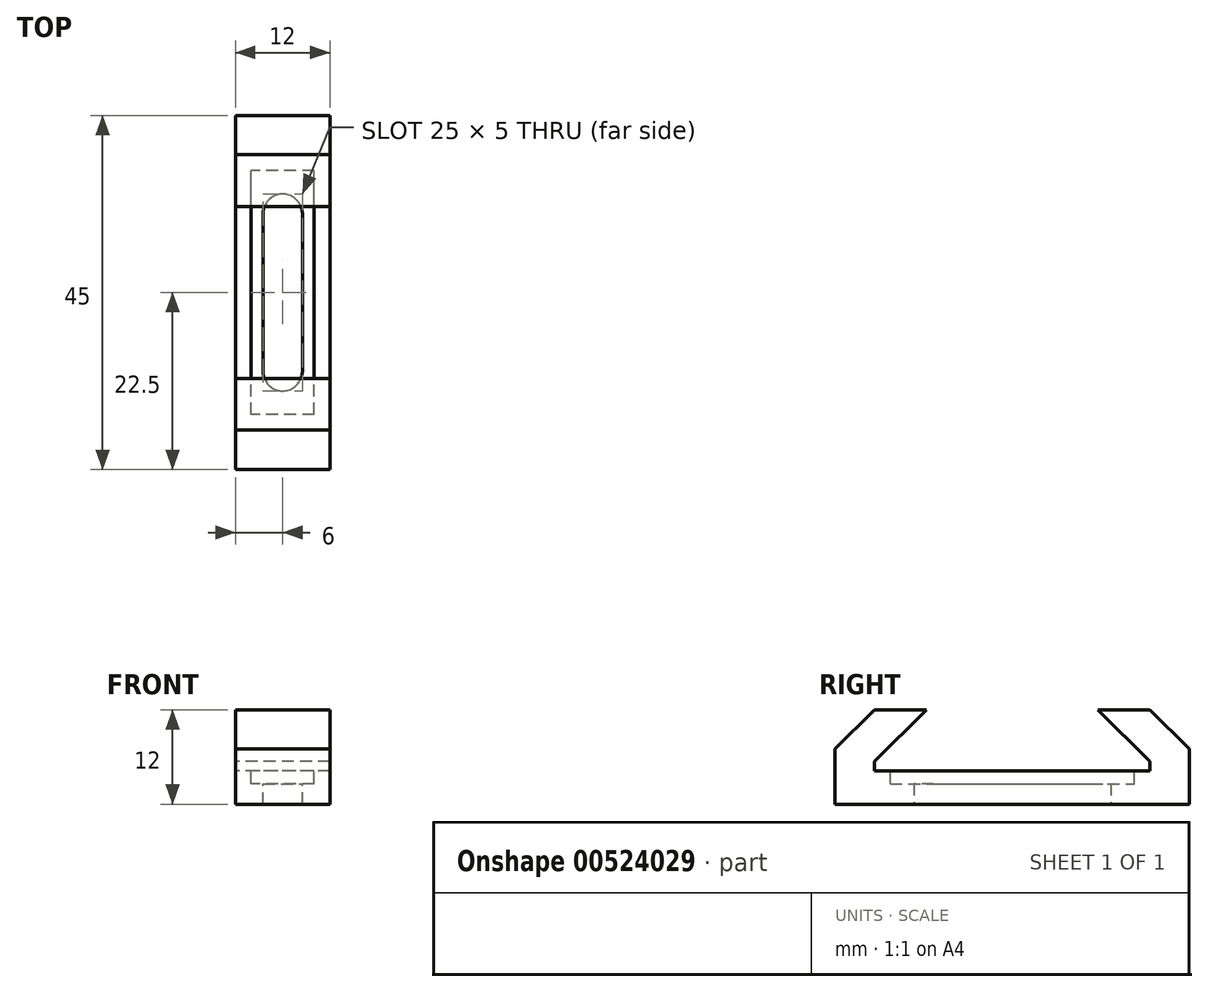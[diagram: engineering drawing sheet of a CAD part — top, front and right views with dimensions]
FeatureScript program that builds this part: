
annotation { "Feature Type Name" : "Feature", "Feature Type Description" : "" }
export const myFeature = defineFeature(function(context is Context, id is Id, definition is map)
    precondition{}
    {
        {
            var Q0;
            Q0=qCreatedBy(makeId("Top.planeOp"),FACE);
            var sketch = newSketch(context, id + "F0", { "sketchPlane" : qUnion([Q0])});
            skLineSegment(sketch, "E0.bottom", {"start": v(6, -22.5) * mm, "end": v(-6, -22.5) * mm});
            skLineSegment(sketch, "E0.top", {"start": v(6, 22.5) * mm, "end": v(-6, 22.5) * mm});
            skLineSegment(sketch, "E0.left", {"start": v(6, -22.5) * mm, "end": v(6, 22.5) * mm});
            skLineSegment(sketch, "E0.right", {"start": v(-6, -22.5) * mm, "end": v(-6, 22.5) * mm});
            skPoint(sketch, "E0.middle", {"position": v(0, 0) * mm});
            skSolve(sketch);
        }
        {
            var Q0;
            Q0=makeQuery(id+"F0.imprint","IMPRINT",FACE,{"disambiguationData":[TD([[makeQuery(id+"F0.imprint","IMPRINT",EDGE,{"derivedFrom":sQuery(id+"F0.wireOp",EDGE,"E0.bottom")}),-1.0]])]});
            extrude(context, id + "F1", {"entities" : qUnion([Q0]), "depth" : 12 * mm, "offsetDistance" : 25 * mm});
        }
        {
            var Q0;
            Q0=makeQuery(id+"F1.opExtrude","SWEPT_FACE",FACE,{"disambiguationData":[OSD([sQuery(id+"F0.wireOp",EDGE,"E0.right")])]});
            var sketch = newSketch(context, id + "F2", { "sketchPlane" : qUnion([Q0])});
            skLineSegment(sketch, "E1.bottom", {"start": v(17.5, 4.2) * mm, "end": v(-17.5, 4.2) * mm});
            skLineSegment(sketch, "E1.top", {"start": v(17.5, 5.4) * mm, "end": v(-17.5, 5.4) * mm});
            skLineSegment(sketch, "E1.left", {"start": v(17.5, 4.2) * mm, "end": v(17.5, 5.4) * mm});
            skLineSegment(sketch, "E1.right", {"start": v(-17.5, 4.2) * mm, "end": v(-17.5, 5.4) * mm});
            skPoint(sketch, "E1.middle", {"position": v(0, 4.8) * mm});
            skLineSegment(sketch, "E2", {"start": v(-17.5, 5.4) * mm, "end": v(-10.9, 12) * mm});
            skLineSegment(sketch, "E3", {"start": v(17.5, 5.4) * mm, "end": v(10.9, 12) * mm});
            skSolve(sketch);
        }
        {
            var Q0;
            Q0=makeQuery(id+"F2.imprint","IMPRINT",FACE,{"disambiguationData":[TD([[makeQuery(id+"F2.imprint","IMPRINT",EDGE,{"derivedFrom":sQuery(id+"F2.wireOp",EDGE,"E1.top")}),-1.0]])]});
            var Q1;
            Q1=makeQuery(id+"F2.imprint","IMPRINT",FACE,{"disambiguationData":[TD([[makeQuery(id+"F2.imprint","IMPRINT",EDGE,{"derivedFrom":sQuery(id+"F2.wireOp",EDGE,"E1.bottom")}),-1.0]])]});
            extrude(context, id + "F3", {"entities" : qUnion([Q0, Q1]), "operationType" : NewBodyOperationType.REMOVE, "endBound" : BoundingType.UP_TO_NEXT, "oppositeDirection" : true, "depth" : 25 * mm, "offsetDistance" : 25 * mm});
        }
        {
            var Q0;
            Q0=makeQuery(id+"F1.opExtrude","CAP_EDGE",EDGE,{"disambiguationData":[OSD([sQuery(id+"F0.wireOp",EDGE,"E0.top")])],"isStart":false});
            var Q1;
            Q1=makeQuery(id+"F1.opExtrude","CAP_EDGE",EDGE,{"disambiguationData":[OSD([sQuery(id+"F0.wireOp",EDGE,"E0.bottom")])],"isStart":false});
            chamfer(context, id + "F4", {"entities" : qUnion([Q0, Q1]), "width" : 5 * mm, "tangentPropagation" : true});
        }
        {
            var Q0;
            Q0=makeQuery(id+"F3.boolean.opBoolean","COPY",FACE,{"derivedFrom":makeQuery(id+"F3.opExtrude","SWEPT_FACE",FACE,{"disambiguationData":[OSD([sQuery(id+"F2.wireOp",EDGE,"E1.bottom")])]})});
            var sketch = newSketch(context, id + "F5", { "sketchPlane" : qUnion([Q0])});
            skLineSegment(sketch, "E4.bottom", {"start": v(4, -15.5) * mm, "end": v(-4, -15.5) * mm});
            skLineSegment(sketch, "E4.top", {"start": v(4, 15.5) * mm, "end": v(-4, 15.5) * mm});
            skLineSegment(sketch, "E4.left", {"start": v(4, -15.5) * mm, "end": v(4, 15.5) * mm});
            skLineSegment(sketch, "E4.right", {"start": v(-4, -15.5) * mm, "end": v(-4, 15.5) * mm});
            skPoint(sketch, "E4.middle", {"position": v(0, 0) * mm});
            skSolve(sketch);
        }
        {
            var Q0;
            Q0=makeQuery(id+"F5.imprint","IMPRINT",FACE,{"disambiguationData":[TD([[makeQuery(id+"F5.imprint","IMPRINT",EDGE,{"derivedFrom":sQuery(id+"F5.wireOp",EDGE,"E4.bottom")}),-1.0]])]});
            extrude(context, id + "F6", {"entities" : qUnion([Q0]), "operationType" : NewBodyOperationType.REMOVE, "oppositeDirection" : true, "depth" : 1.6 * mm, "offsetDistance" : 25 * mm});
        }
        {
            var Q0;
            Q0=makeQuery(id+"F6.boolean.opBoolean","COPY",FACE,{"derivedFrom":makeQuery(id+"F6.opExtrude","CAP_FACE",FACE,{"disambiguationData":[OSD([sQuery(id+"F5.wireOp",EDGE,"E4.bottom"),sQuery(id+"F5.wireOp",EDGE,"E4.top"),sQuery(id+"F5.wireOp",EDGE,"E4.left"),sQuery(id+"F5.wireOp",EDGE,"E4.right")])],"isStart":false})});
            var sketch = newSketch(context, id + "F7", { "sketchPlane" : qUnion([Q0])});
            skLineSegment(sketch, "E5.bottom", {"start": v(2.5, -12.5) * mm, "end": v(-2.5, -12.5) * mm});
            skLineSegment(sketch, "E5.top", {"start": v(2.5, 12.5) * mm, "end": v(-2.5, 12.5) * mm});
            skLineSegment(sketch, "E5.left", {"start": v(2.5, -12.5) * mm, "end": v(2.5, 12.5) * mm});
            skLineSegment(sketch, "E5.right", {"start": v(-2.5, -12.5) * mm, "end": v(-2.5, 12.5) * mm});
            skPoint(sketch, "E5.middle", {"position": v(0, 0) * mm});
            skSolve(sketch);
        }
        {
            var Q0;
            Q0=makeQuery(id+"F7.imprint","IMPRINT",FACE,{"disambiguationData":[TD([[makeQuery(id+"F7.imprint","IMPRINT",EDGE,{"derivedFrom":sQuery(id+"F7.wireOp",EDGE,"E5.bottom")}),-1.0]])]});
            extrude(context, id + "F8", {"entities" : qUnion([Q0]), "operationType" : NewBodyOperationType.REMOVE, "endBound" : BoundingType.UP_TO_NEXT, "oppositeDirection" : true, "depth" : 25 * mm, "offsetDistance" : 25 * mm});
        }
        {
            var Q0;
            Q0=makeQuery(id+"F8.boolean.opBoolean","COPY",EDGE,{"derivedFrom":makeQuery(id+"F8.opExtrude","SWEPT_EDGE",EDGE,{"disambiguationData":[OSD([sQuery(id+"F7.wireOp",EDGE,"E5.top"),sQuery(id+"F7.wireOp",EDGE,"E5.left")])]})});
            var Q1;
            Q1=makeQuery(id+"F8.boolean.opBoolean","COPY",EDGE,{"derivedFrom":makeQuery(id+"F8.opExtrude","SWEPT_EDGE",EDGE,{"disambiguationData":[OSD([sQuery(id+"F7.wireOp",EDGE,"E5.top"),sQuery(id+"F7.wireOp",EDGE,"E5.right")])]})});
            var Q2;
            Q2=makeQuery(id+"F8.boolean.opBoolean","COPY",EDGE,{"derivedFrom":makeQuery(id+"F8.opExtrude","SWEPT_EDGE",EDGE,{"disambiguationData":[OSD([sQuery(id+"F7.wireOp",EDGE,"E5.bottom"),sQuery(id+"F7.wireOp",EDGE,"E5.right")])]})});
            var Q3;
            Q3=makeQuery(id+"F8.boolean.opBoolean","COPY",EDGE,{"derivedFrom":makeQuery(id+"F8.opExtrude","SWEPT_EDGE",EDGE,{"disambiguationData":[OSD([sQuery(id+"F7.wireOp",EDGE,"E5.bottom"),sQuery(id+"F7.wireOp",EDGE,"E5.left")])]})});
            fillet(context, id + "F9", {"entities" : qUnion([Q0, Q1, Q2, Q3]), "radius" : 2.5 * mm, "tangentPropagation" : true, "allowEdgeOverflow" : false});
        }
    });
